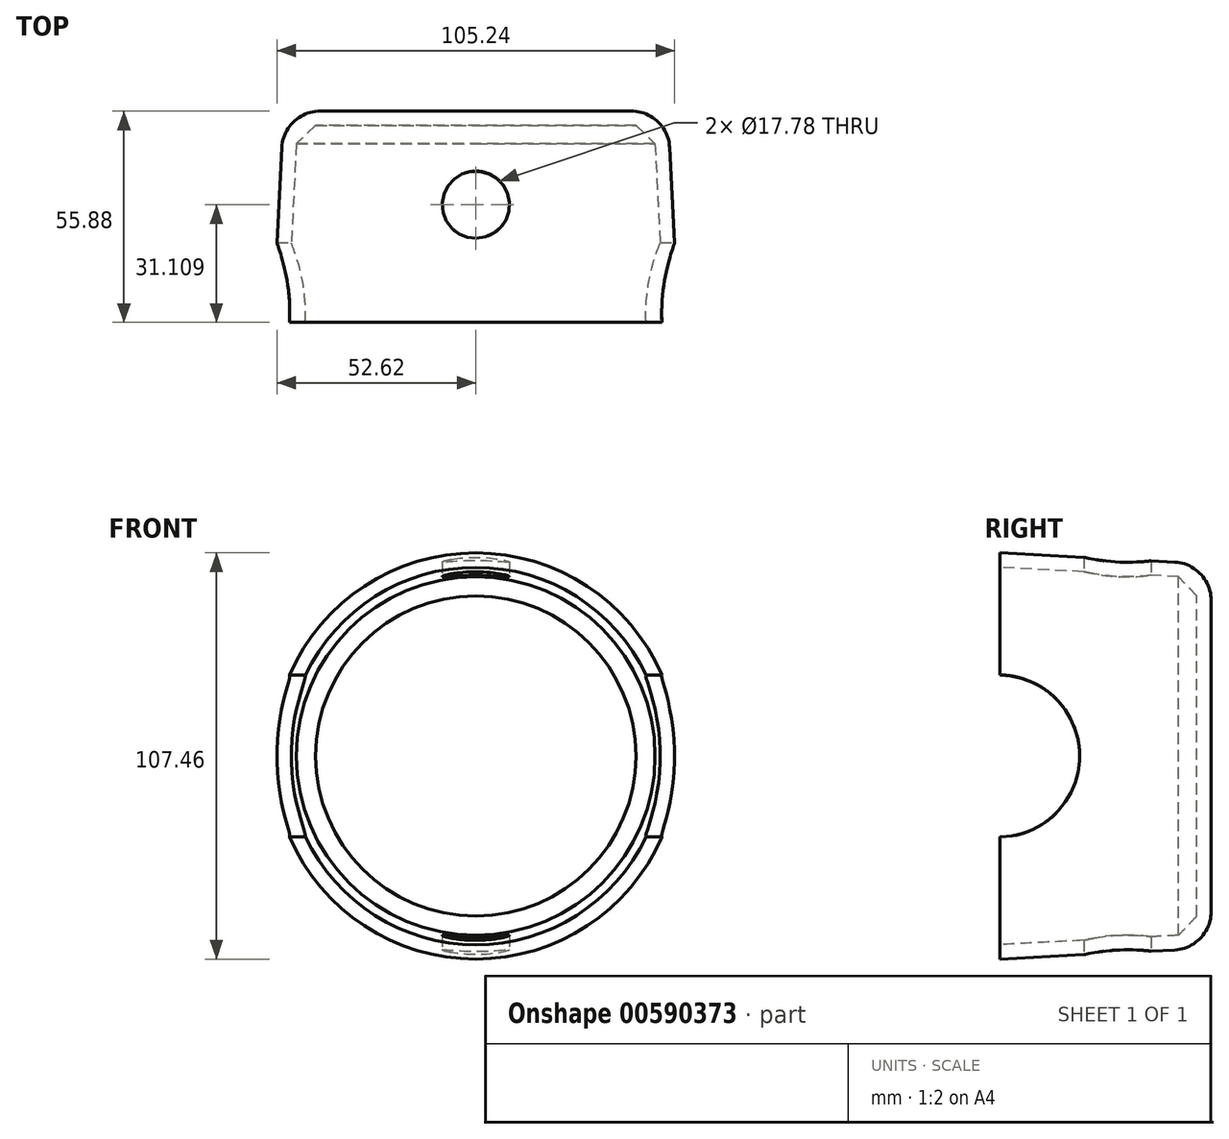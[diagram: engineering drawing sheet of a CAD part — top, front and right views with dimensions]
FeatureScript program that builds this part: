
annotation { "Feature Type Name" : "Feature", "Feature Type Description" : "" }
export const myFeature = defineFeature(function(context is Context, id is Id, definition is map)
    precondition{}
    {
        {
            var Q0;
            Q0=qCreatedBy(makeId("Front.planeOp"),FACE);
            var sketch = newSketch(context, id + "F0", { "sketchPlane" : qUnion([Q0])});
            skCircle(sketch, "E0", {"center": v(0, 0) * mm, "radius": 50.8 * mm});
            skSolve(sketch);
        }
        {
            var Q0;
            Q0=makeQuery(id+"F0.imprint","IMPRINT",FACE,{"disambiguationData":[TD([[makeQuery(id+"F0.imprint","IMPRINT",EDGE,{"derivedFrom":sQuery(id+"F0.wireOp",EDGE,"E0")}),1.0]])]});
            extrude(context, id + "F1", {"entities" : qUnion([Q0]), "depth" : 55.88 * mm, "offsetDistance" : 25.4 * mm, "hasDraft" : true, "draftAngle" : 3 * degree});
        }
        {
            var Q0;
            Q0=makeQuery(id+"F1.opExtrude","CAP_FACE",FACE,{"disambiguationData":[OSD([sQuery(id+"F0.wireOp",EDGE,"E0")])],"isStart":false});
            shell(context, id + "F2", {"entities" : qUnion([Q0]), "thickness" : 3.8 * mm});
        }
        {
            var Q0;
            Q0=qCreatedBy(makeId("Front.planeOp"),FACE);
            cPlane(context, id + "F3", {"entities" : qUnion([Q0]), "cplaneType" : CPlaneType.OFFSET, "offset" : 55.88 * mm, "width" : 152.4 * mm, "height" : 152.4 * mm});
        }
        {
            var Q0;
            Q0=qCreatedBy(makeId("Right.planeOp"),FACE);
            var sketch = newSketch(context, id + "F4", { "sketchPlane" : qUnion([Q0])});
            skCircle(sketch, "E1", {"center": v(-56.23, 0) * mm, "radius": 21.45 * mm});
            skSolve(sketch);
        }
        {
            var Q0;
            Q0 = qSketchRegion(id + "F4", true);
            extrude(context, id + "F5", {"entities" : qUnion([Q0]), "operationType" : NewBodyOperationType.REMOVE, "oppositeDirection" : true, "depth" : 58.17 * mm, "offsetDistance" : 25.4 * mm, "hasSecondDirection" : true, "secondDirectionOppositeDirection" : false, "secondDirectionDepth" : 65.8 * mm});
        }
        {
            var Q0;
            Q0=makeQuery(id+"F1.opExtrude","CAP_EDGE",EDGE,{"disambiguationData":[OSD([sQuery(id+"F0.wireOp",EDGE,"E0")])],"isStart":true});
            fillet(context, id + "F6", {"entities" : qUnion([Q0]), "radius" : 10.16 * mm, "tangentPropagation" : true, "allowEdgeOverflow" : false});
        }
        {
            var Q0;
            {var subQ0=sQuery(id+"F0.wireOp",EDGE,"E0");Q0=makeQuery(id+"F2.opShell","OFFSET_EDGE",EDGE,{"disambiguationData":[OSD([subQ0]),TDD([makeQuery(id+"F1.opExtrude","CAP_EDGE",EDGE,{"disambiguationData":[OSD([subQ0])],"isStart":true})])]});}
            chamfer(context, id + "F7", {"entities" : qUnion([Q0]), "width" : 5.08 * mm, "tangentPropagation" : true});
        }
        {
            var Q0;
            Q0=qCreatedBy(makeId("Top.planeOp"),FACE);
            cPlane(context, id + "F8", {"entities" : qUnion([Q0]), "cplaneType" : CPlaneType.OFFSET, "offset" : 64 * mm, "oppositeDirection" : true, "width" : 152.4 * mm, "height" : 152.4 * mm});
        }
        {
            var Q0;
            Q0=qCreatedBy(id+"F8.planeOp",FACE);
            var sketch = newSketch(context, id + "F9", { "sketchPlane" : qUnion([Q0])});
            skCircle(sketch, "E2", {"center": v(0, -24.77) * mm, "radius": 8.9 * mm});
            skSolve(sketch);
        }
        {
            var Q0;
            Q0 = qSketchRegion(id + "F9", true);
            extrude(context, id + "F10", {"entities" : qUnion([Q0]), "operationType" : NewBodyOperationType.REMOVE, "depth" : 133.86 * mm, "offsetDistance" : 25.4 * mm});
        }
    });
